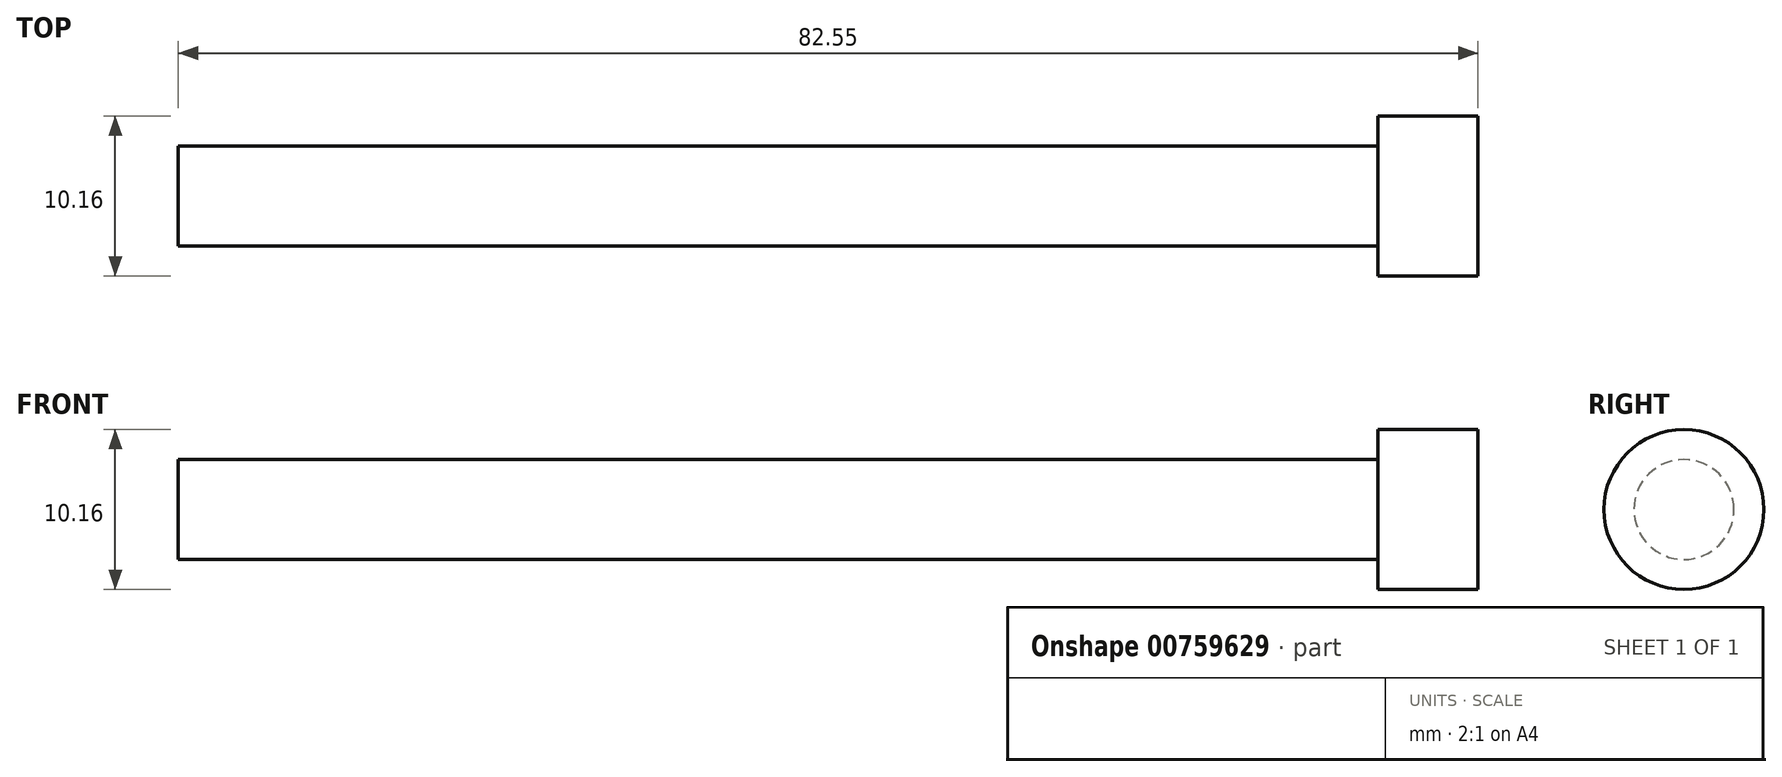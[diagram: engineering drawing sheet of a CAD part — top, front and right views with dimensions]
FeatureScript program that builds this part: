
annotation { "Feature Type Name" : "Feature", "Feature Type Description" : "" }
export const myFeature = defineFeature(function(context is Context, id is Id, definition is map)
    precondition{}
    {
        {
            var Q0;
            Q0=qCreatedBy(makeId("Right.planeOp"),FACE);
            var sketch = newSketch(context, id + "F0", { "sketchPlane" : qUnion([Q0])});
            skCircle(sketch, "E0", {"center": v(0, 0) * mm, "radius": 3.18 * mm});
            skSolve(sketch);
        }
        {
            var Q0;
            Q0=makeQuery(id+"F0.imprint","IMPRINT",FACE,{"disambiguationData":[TD([[makeQuery(id+"F0.imprint","IMPRINT",EDGE,{"derivedFrom":sQuery(id+"F0.wireOp",EDGE,"E0")}),1.0]])]});
            extrude(context, id + "F1", {"entities" : qUnion([Q0]), "endBound" : BoundingType.SYMMETRIC, "depth" : 76.2 * mm, "offsetDistance" : 25.4 * mm});
        }
        {
            var Q0;
            Q0=makeQuery(id+"F1.opExtrude","CAP_FACE",FACE,{"disambiguationData":[OSD([sQuery(id+"F0.wireOp",EDGE,"E0")])],"isStart":false});
            var sketch = newSketch(context, id + "F2", { "sketchPlane" : qUnion([Q0])});
            skCircle(sketch, "E1", {"center": v(0, 0) * mm, "radius": 5.08 * mm});
            skSolve(sketch);
        }
        {
            var Q0;
            Q0=makeQuery(id+"F2.imprint","IMPRINT",FACE,{"disambiguationData":[TD([[makeQuery(id+"F2.imprint","IMPRINT",EDGE,{"derivedFrom":sQuery(id+"F2.wireOp",EDGE,"E1")}),1.0]])]});
            var Q1;
            Q1=makeQuery(id+"F2.imprint","IMPRINT",FACE,{"disambiguationData":[TD([[makeQuery(id+"F2.imprint","IMPRINT",EDGE,{"derivedFrom":makeQuery(id+"F1.opExtrude","CAP_EDGE",EDGE,{"disambiguationData":[OSD([sQuery(id+"F0.wireOp",EDGE,"E0")])],"isStart":false})}),1.0]])]});
            extrude(context, id + "F3", {"entities" : qUnion([Q0, Q1]), "operationType" : NewBodyOperationType.ADD, "depth" : 6.35 * mm, "offsetDistance" : 25.4 * mm});
        }
    });
